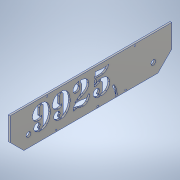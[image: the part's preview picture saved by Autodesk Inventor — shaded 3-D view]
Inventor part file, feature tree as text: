
AUTODESK INVENTOR PART (.ipt)
format: ipt  version: 2021 (Build 250183000, 183)  size: 489,984 bytes
history: native  units: in
note: dims shown in document units (in); Inventor stores cm internally (conversion verified against a paired STEP export)
features: sketch x5, extrude x4, chamfer x2, hole x2, projected_geometry x1
ambient origin geometry x8: Origin, YZ Plane, XZ Plane, XY Plane, X Axis, Y Axis, Z Axis, Center Point
bodies: Solid1 (feature_tree)
feature tree (14):
  extrude  "Extrusion1"  Depth=17.5in
  chamfer  "Chamfer1"  Distance=0.1875in
  chamfer  "Chamfer2"  Distance=1.5in Angle=45.0deg
  hole  "Hole3"  [1 undecoded]
  sketch  "Sketch9"  dims[d3=1.25in]
  hole  "Hole4"  [1 undecoded]
  extrude  "Extrusion6"  Depth=0.125in
  extrude  "Extrusion7"  Depth=0.603in
  extrude  "Extrusion8"  Depth=0.125in
  sketch  "Sketch1"  dims[d0=4.0in d1=17.5in]
  sketch  "Sketch8"  dims[d2=0.501in]
  projected_geometry  "Projected Loop7"
  sketch  "Sketch10"  dims[d4=2.0in]
  sketch  "Sketch11"  dims[d5=2.0in d6=0.1875in d7=0.0in d8=1.5in d9=0.125in d10=45.0deg d11=1.5in d12=0.125in d13=45.0deg d22=6.517in d23=0.125in d24=0.603in d25=0.125in d26=0.63in d27=6.517in d28=0.125in d29=0.603in d30=6.517in d31=0.125in d32=0.63in d33=6.517in d110=0.175in d111=0.175in d112=4.0in d113=4.0in d114=0.175in d115=0.175in d116=0.15in d117=0.75in d118=0.375in d119=0.25in d120=0.5635in d121=1.0in d122=0.8108in d123=5.0in d124=5.0in d125=8.0in d126=0.15in d127=0.2in d128=0.75in d129=0.375in d130=0.25in d131=0.5635in d132=1.0in d133=0.8108in d134=2.0in d135=0.2in d137=1.0in d138=0.0in d139=0.2in d140=1.0in d141=1.0in d142=0.0in d143=0.75in d144=0.75in d145=0.6033in d146=4.0in d147=0.0in d148=0.0in]
note: 2 required parameter values undecoded (feature->parameter linkage not recoverable at this tier; creation-order binding heuristic only, values carry confidence <= 0.55)
